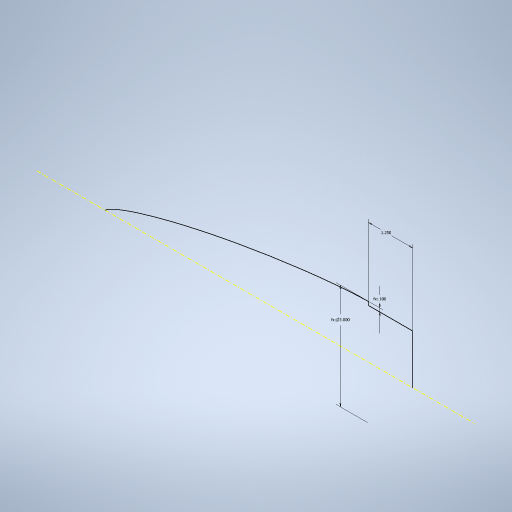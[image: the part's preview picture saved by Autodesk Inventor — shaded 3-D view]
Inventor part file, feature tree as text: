
AUTODESK INVENTOR PART (.ipt)
format: ipt  version: 2024 (Build 280153000, 153)  size: 239,104 bytes
history: native  units: in
note: dims shown in document units (in); Inventor stores cm internally (conversion verified against a paired STEP export)
features: sketch x1, other x1
ambient origin geometry x8: Origin, YZ Plane, XZ Plane, XY Plane, X Axis, Y Axis, Z Axis, Center Point
feature tree (2):
  sketch  "Sketch1"  dims[d0=0.0in d1=7.5in d2=3.0in d3=1.25in d4=0.1in]
  other  "2D Equation Curve1"
